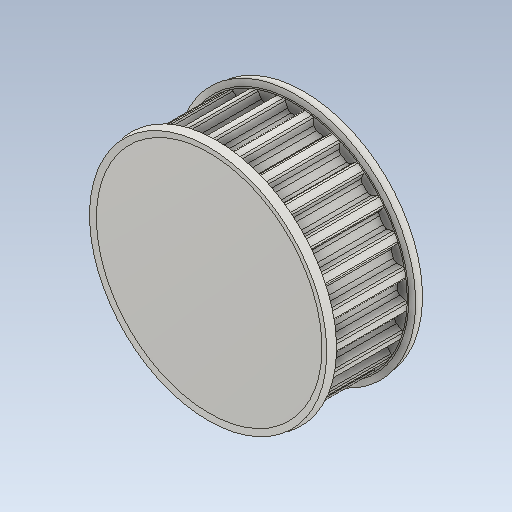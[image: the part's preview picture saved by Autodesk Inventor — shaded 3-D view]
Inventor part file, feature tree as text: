
AUTODESK INVENTOR PART (.ipt)
format: ipt  version: 2020 (Build 240168000, 168)  size: 454,656 bytes
history: native  units: mm (DEFAULTED — no unit token found)
features: other x3, extrude x2, fillet x1, pattern_circular x1
ambient origin geometry x8: Origin, YZ Plane, XZ Plane, XY Plane, X Axis, Y Axis, Z Axis, Center Point
bodies: Solid1 (feature_tree)
feature tree (7):
  other  "Pulley Sketch"
  extrude  "Base Body"  Depth=16.170142mm
  extrude  "Tooth"  Depth=0.254mm
  fillet  "Tooth Fillet"  Radius=0.6858mm
  pattern_circular  "Teeth"  [2 undecoded]
  other  "Left flange"
  other  "Right flange"
note: 2 required parameter values undecoded (feature->parameter linkage not recoverable at this tier; creation-order binding heuristic only, values carry confidence <= 0.55)
